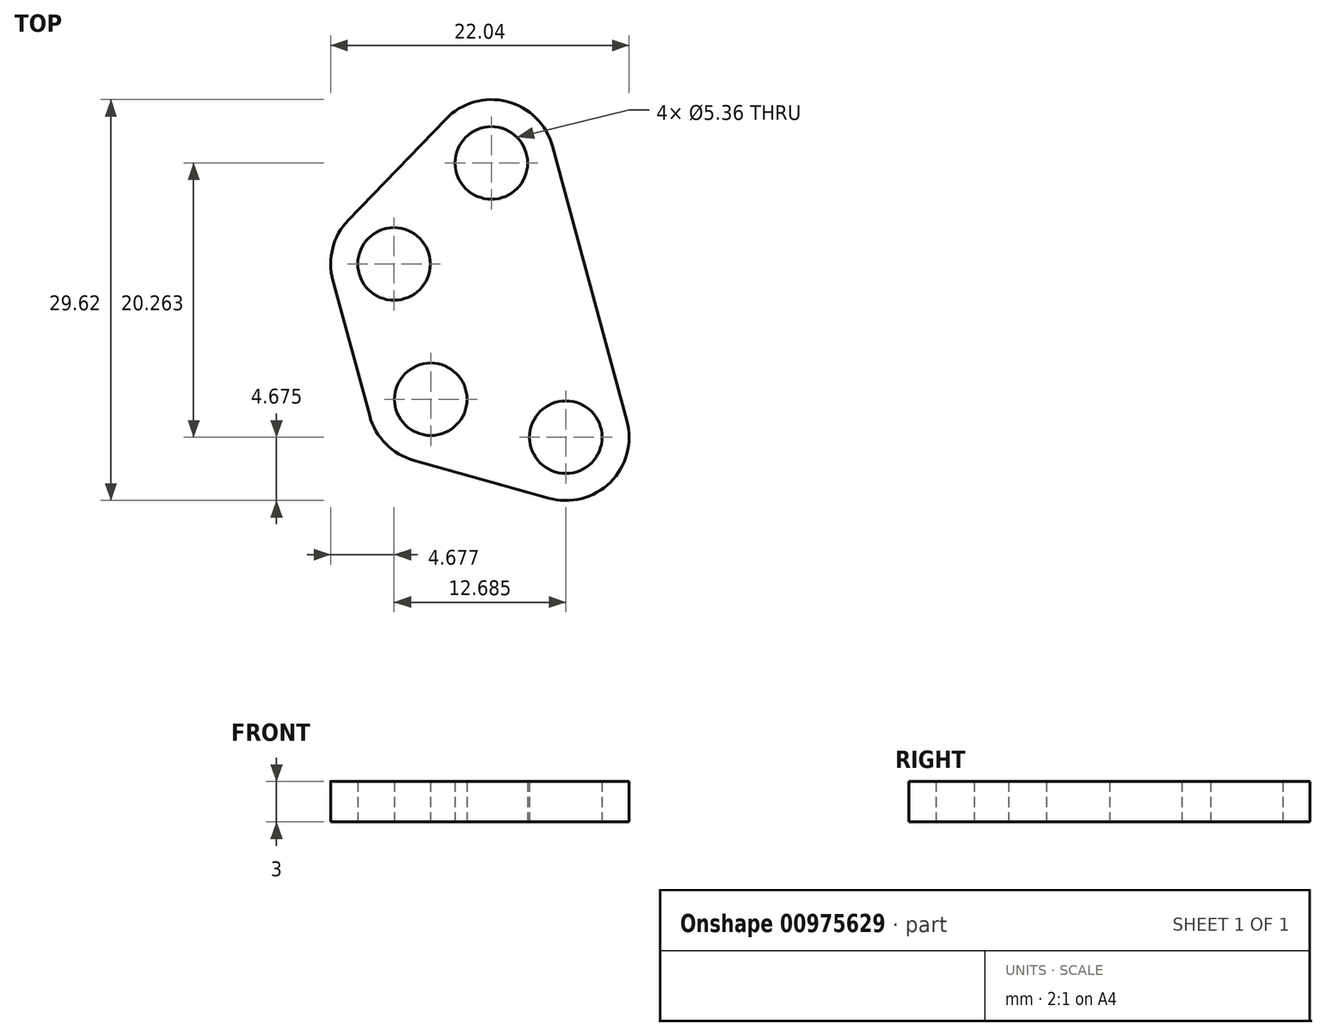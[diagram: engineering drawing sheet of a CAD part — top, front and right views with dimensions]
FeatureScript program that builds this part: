
annotation { "Feature Type Name" : "Feature", "Feature Type Description" : "" }
export const myFeature = defineFeature(function(context is Context, id is Id, definition is map)
    precondition{}
    {
        {
            var Q0;
            Q0=qCreatedBy(makeId("Top.planeOp"), FACE);
            var sketch = newSketch(context, id + "F0", { "sketchPlane" : qUnion([Q0])});
            skCircle(sketch, "E0", {"center": v(0, 0) * mm, "radius": 2.68 * mm});
            skCircle(sketch, "E1", {"center": v(9.97, -2.8) * mm, "radius": 2.68 * mm});
            skCircle(sketch, "E2", {"center": v(-2.71, 10) * mm, "radius": 2.68 * mm});
            skCircle(sketch, "E3", {"center": v(4.47, 17.46) * mm, "radius": 2.68 * mm});
            skLineSegment(sketch, "E4", {"start": v(4.82, 22) * mm, "end": v(8.7, 7.67) * mm, "construction": true});
            skLineSegment(sketch, "E5", {"start": v(0, 0) * mm, "end": v(-2.71, 10) * mm, "construction": true});
            skCircle(sketch, "E6", {"center": v(-2.71, 10) * mm, "radius": 4.68 * mm});
            skLineSegment(sketch, "E7", {"start": v(0, 0) * mm, "end": v(98.5, -68.5) * mm, "construction": true});
            skCircle(sketch, "E8", {"center": v(9.97, -2.8) * mm, "radius": 4.68 * mm});
            skCircle(sketch, "E9", {"center": v(4.47, 17.46) * mm, "radius": 4.68 * mm});
            skLineSegment(sketch, "E10", {"start": v(9.97, -2.8) * mm, "end": v(4.47, 17.46) * mm, "construction": true});
            skLineSegment(sketch, "E11", {"start": v(7.22, 7.33) * mm, "end": v(-1.36, 5) * mm, "construction": true});
            skLineSegment(sketch, "E12", {"start": v(9.97, -2.8) * mm, "end": v(74.42, -76.46) * mm, "construction": true});
            skCircle(sketch, "E13", {"center": v(0, 0) * mm, "radius": 4.68 * mm});
            skSolve(sketch);
        }
        {
            var Q0;
            Q0=qCreatedBy(makeId("Top.planeOp"), FACE);
            var sketch = newSketch(context, id + "F1", { "sketchPlane" : qUnion([Q0])});
            skLineSegment(sketch, "E14", {"start": v(-6.08, 13.24) * mm, "end": v(1.1, 20.7) * mm});
            skLineSegment(sketch, "E15", {"start": v(9, 18.68) * mm, "end": v(14.49, -1.58) * mm});
            skLineSegment(sketch, "E16", {"start": v(8.7, -7.3) * mm, "end": v(-1.27, -4.5) * mm});
            skPoint(sketch, "E17.visualSharp", {"position": v(16.65, -9.54) * mm});
            skArc(sketch, "E17.filletArc", {"start": v(8.7, -7.3) * mm, "mid": v(13.27, -6.13) * mm, "end": v(14.49, -1.58) * mm});
            skPoint(sketch, "E18.visualSharp", {"position": v(6.83, 26.65) * mm});
            skArc(sketch, "E18.filletArc", {"start": v(9, 18.68) * mm, "mid": v(5.64, 22) * mm, "end": v(1.1, 20.7) * mm});
            skLineSegment(sketch, "E19.filletArc", {"start": v(-6.08, 13.24) * mm, "end": v(-6.08, 13.24) * mm});
            skCircle(sketch, "E20.0", {"center": v(4.47, 17.46) * mm, "radius": 2.68 * mm});
            skCircle(sketch, "E20.1", {"center": v(-2.71, 10) * mm, "radius": 2.68 * mm});
            skCircle(sketch, "E20.2", {"center": v(0, 0) * mm, "radius": 2.68 * mm});
            skCircle(sketch, "E21.0", {"center": v(9.97, -2.8) * mm, "radius": 2.68 * mm});
            skLineSegment(sketch, "E22", {"start": v(-7.23, 8.77) * mm, "end": v(-4.52, -1.23) * mm});
            skArc(sketch, "E23", {"start": v(-7.23, 8.77) * mm, "mid": v(-7.25, 11.16) * mm, "end": v(-6.08, 13.24) * mm});
            skArc(sketch, "E24", {"start": v(-4.52, -1.23) * mm, "mid": v(-3.32, -3.3) * mm, "end": v(-1.27, -4.5) * mm});
            skSolve(sketch);
        }
        {
            var Q0;
            Q0 = qSketchRegion(id + "F1", true);
            extrude(context, id + "F2", {"entities" : qUnion([Q0]), "domain" : OperationDomain.MODEL, "flatOperationType" : FlatOperationType.REMOVE, "depth" : 3 * mm, "offsetDistance" : 25 * mm});
        }
    });
